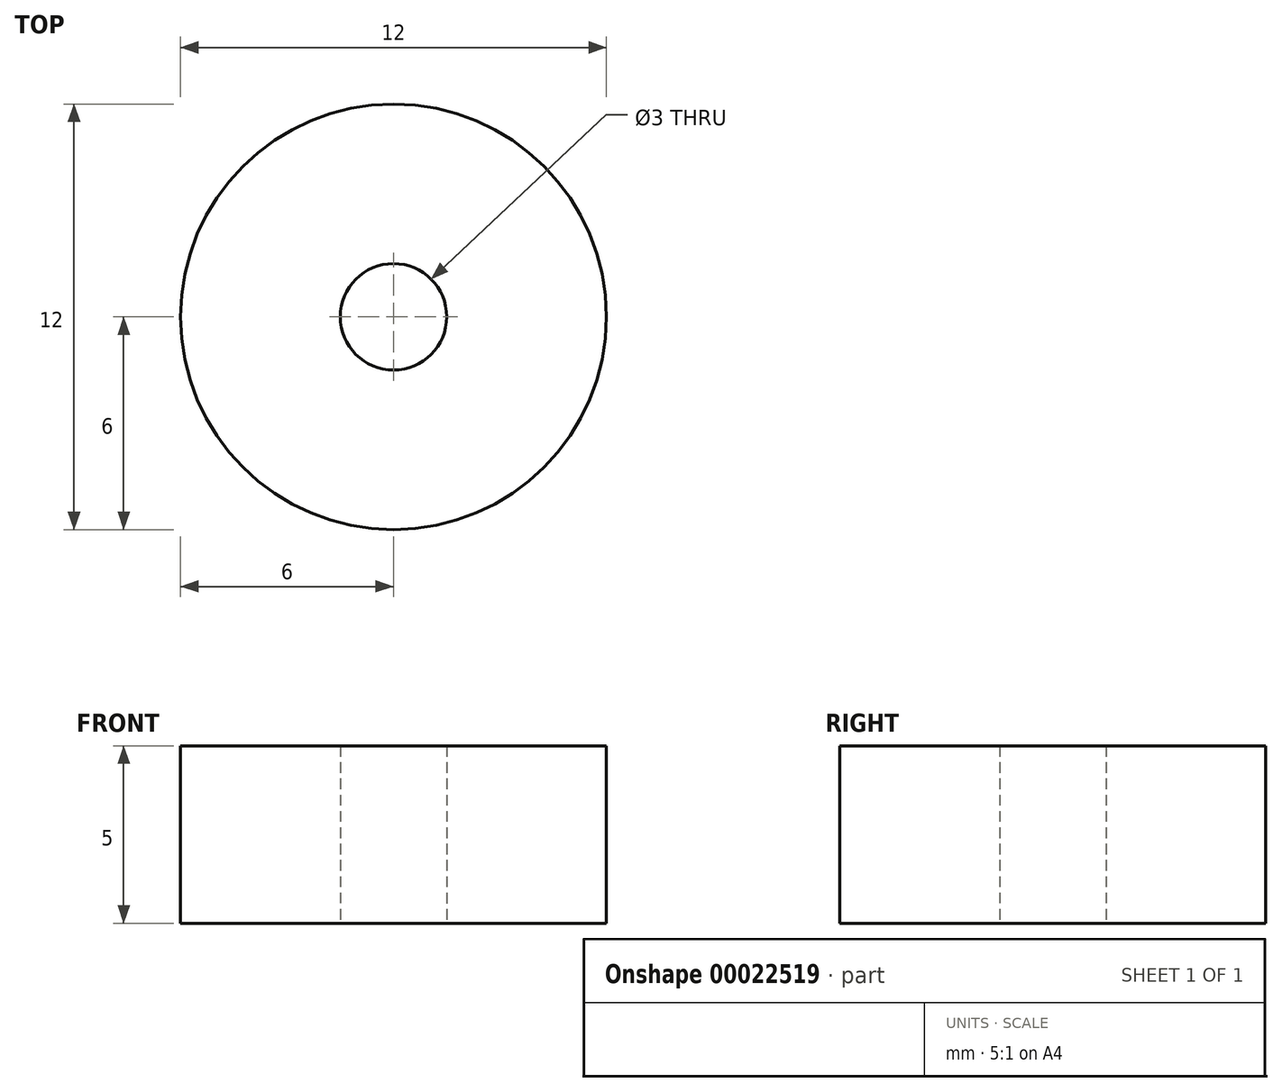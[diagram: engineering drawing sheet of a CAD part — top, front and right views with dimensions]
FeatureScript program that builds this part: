
annotation { "Feature Type Name" : "Feature", "Feature Type Description" : "" }
export const myFeature = defineFeature(function(context is Context, id is Id, definition is map)
    precondition{}
    {
        {
            var Q0;
            Q0=qCreatedBy(makeId("Top.planeOp"),FACE);
            var sketch = newSketch(context, id + "F0", { "sketchPlane" : qUnion([Q0])});
            skCircle(sketch, "E0", {"center": v(0, 0) * mm, "radius": 6 * mm});
            skCircle(sketch, "E1", {"center": v(0, 0) * mm, "radius": 1.5 * mm});
            skSolve(sketch);
        }
        {
            var Q0;
            Q0=makeQuery(id+"F0.imprint","IMPRINT",FACE,{"disambiguationData":[TD([[makeQuery(id+"F0.imprint","IMPRINT",EDGE,{"derivedFrom":sQuery(id+"F0.wireOp",EDGE,"E0")}),1.0]])]});
            extrude(context, id + "F1", {"entities" : qUnion([Q0]), "depth" : 5 * mm});
        }
    });
